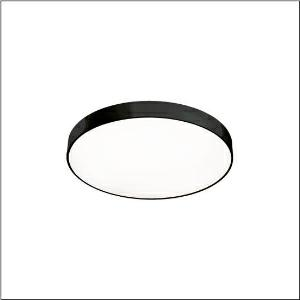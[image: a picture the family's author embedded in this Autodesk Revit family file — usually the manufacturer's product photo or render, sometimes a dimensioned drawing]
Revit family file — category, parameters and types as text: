
# Revit family: round_21_m_51mr36gm8321b
name_source: partatom
category: Lighting Fixtures
units: mm (PartAtom-declared; Revit-internal decimal feet)

## family parameters
Cut with Voids When Loaded = No
Host = Face
Light Source = No
Part Type = Normal
Room Calculation Point = No
Round Connector Dimension = Use Diameter
Shared = No

## types (1)
- --- (1 x LED, 8610 lm, 62.3 W, 3000K)
    Apparent Load = 62 VA
    CIE Flux Codes = 49 80 96 85 100
    Color Rendering = 80
    Color Temperature = 3000K
    Default Elevation = 1800 mm
    Description = Round 21 M, wall and ceiling luminaire, primary optical cover: cover, of PMMA, opal, light emission: direct/indirect distribution, primary light characteristic: symmetric, installation type: suspended mounting, surface-mounted, LED, rated luminous flux: 8.600lm, luminous efficacy: 138lm/W, light colour: 830, colour temperature: 3000K, control gear: ON/OFF Multilumen, with terminal, 3-pole, mains connection: 230V, AC, 50/60Hz, rated input power: 62.3W, housing, of aluminium, coated, black, diameter: 600mm, height: 62mm, protection rating (complete): IP40, insulation class (complete): insulation class I (protective earthing), certification: CE, impact resistance: IK04, permissible operating ambient temperature: -10..+35°C, packaging unit: 1 piece
    Height = 87 mm
    Lamp = 1 x LED
    Lamp Light Flux = 8610 lm
    Lamp Power = 62.3 W
    Lamp count = 1
    Length = 600 mm
    Luminous efficacy = 138 lm/W
    Manufacturer = Siteco
    ModVariant = No
    Model = 51MR36GM8321B
    Mounting Place = Ceiling
    Mounting Type = Surface mounted
    Number of Poles = 1
    OnlyDefault = Yes
    Power Factor = 1
    Product Name = Round 21 M
    Product group = wall and ceiling luminaire | ceiling mounted
    ProductGroupID = 304
    Protection Class = Protection class I
    Protection Degree = IP 40
    RLX_Detail_Level = 1
    RLX_Emergency_Light_Flux = 0 lm
    RLX_Emergency_Type = 0
    RLX_Emergency_Type_DB = No
    RlxData = <blob elided: 20845 chars, md5=16d40f09>
    Socket = socket
    Standby Power = 0 W
    System Light Flux = 8610 lm
    System Power = 62 W
    Type Comments = factory setting: luminous flux: 100 % | (ON | ON | ON | ON) | 700 mA
    Type Image = l_1258332.jpg
    URL = http://relux.com
    VarID = @adj_041183
    Voltage = 0 V
    Weight = 0.00 kg
    Width = 0 mm  [stored 0 ft]

note: [stored X ft] marks values corroborated as IEEE doubles in the binary element streams (Revit-internal decimal feet)

## geometry (parser evidence)
native form markers: Blend x4, Sweep x11
no freeform markers — native parametric forms only
